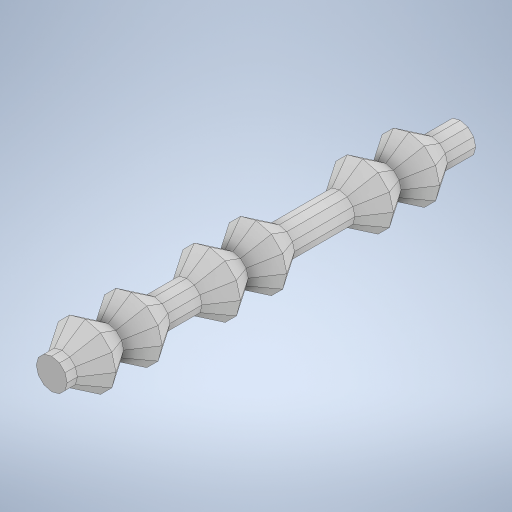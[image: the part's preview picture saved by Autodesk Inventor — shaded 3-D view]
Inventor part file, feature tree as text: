
AUTODESK INVENTOR PART (.ipt)
format: ipt  version: 2023 (Build 270158000, 158)  size: 630,272 bytes
history: native  units: in
note: dims shown in document units (in); Inventor stores cm internally (conversion verified against a paired STEP export)
features: sketch x8, extrude x6, projected_geometry x5, other x4, mirror x4, loft x1, shell x1
ambient origin geometry x8: Origin, YZ Plane, XZ Plane, XY Plane, X Axis, Y Axis, Z Axis, Center Point
bodies: Body1 (feature_tree)
feature tree (29):
  other  "솔리드1"
  sketch  "스케치1"
  other  "작업 평면1"
  loft  "로프트1"
  mirror  "미러1"
  mirror  "미러2"
  extrude  "돌출1"  Depth=0.3543in
  other  "작업 평면2"
  mirror  "미러3"
  extrude  "돌출2"  Depth=0.4724in
  other  "작업 평면6"
  mirror  "미러5"
  extrude  "돌출3"  TaperAngle=0.0deg  [1 undecoded]
  shell  "쉘1"  Thickness=0.0in
  extrude  "돌출4"  Depth=0.9252in TaperAngle=0.0deg
  extrude  "돌출5"  [1 undecoded]
  extrude  "돌출6"  Depth=0.4921in TaperAngle=0.0deg
  sketch  "스케치2"
  sketch  "스케치3"
  projected_geometry  "투영된 루프1"
  sketch  "스케치4"
  projected_geometry  "투영된 루프2"
  sketch  "스케치5"
  projected_geometry  "투영된 루프3"
  sketch  "스케치6"
  projected_geometry  "투영된 루프4"
  sketch  "스케치7"
  sketch  "스케치8"
  projected_geometry  "투영된 루프5"
note: 2 required parameter values undecoded (feature->parameter linkage not recoverable at this tier; creation-order binding heuristic only, values carry confidence <= 0.55)
